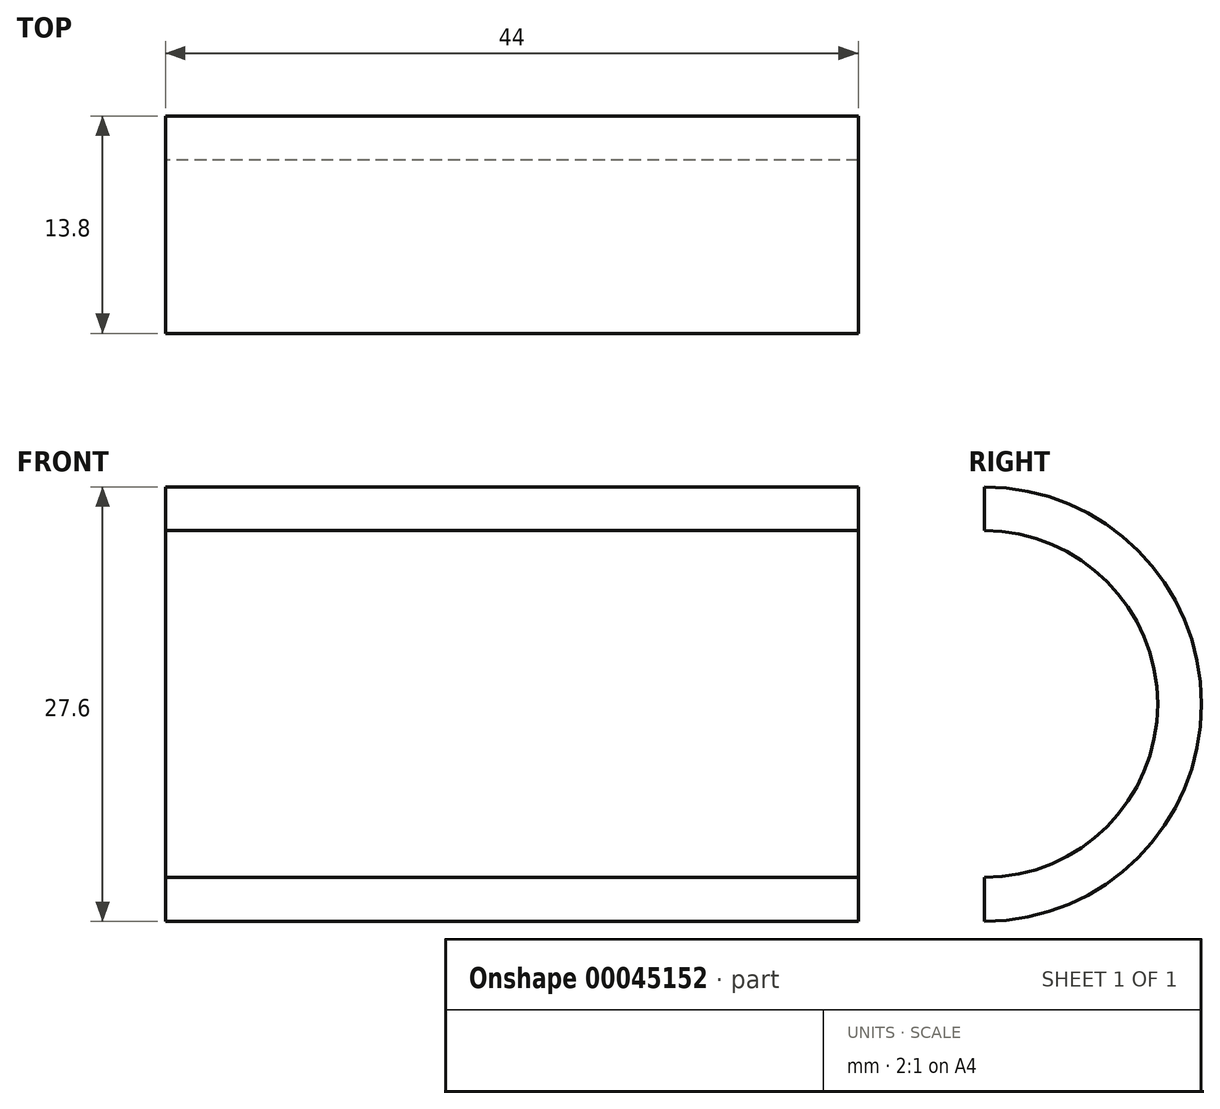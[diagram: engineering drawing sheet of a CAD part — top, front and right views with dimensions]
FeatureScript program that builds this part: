
annotation { "Feature Type Name" : "Feature", "Feature Type Description" : "" }
export const myFeature = defineFeature(function(context is Context, id is Id, definition is map)
    precondition{}
    {
        {
            var Q0;
            Q0=qCreatedBy(makeId("Right.planeOp"),FACE);
            var sketch = newSketch(context, id + "F0", { "sketchPlane" : qUnion([Q0])});
            skArc(sketch, "E0", {"start": v(0, -13.8) * mm, "mid": v(13.8, 0) * mm, "end": v(0, 13.8) * mm});
            skLineSegment(sketch, "E1", {"start": v(0, 13.8) * mm, "end": v(0, -13.8) * mm});
            skLineSegment(sketch, "E2", {"start": v(0, 0) * mm, "end": v(13.8, 0) * mm, "construction": true});
            skSolve(sketch);
        }
        {
            var Q0;
            Q0 = qSketchRegion(id + "F0", true);
            extrude(context, id + "F1", {"entities" : qUnion([Q0]), "depth" : 44 * mm});
        }
        {
            var Q0;
            Q0=qCreatedBy(makeId("Right.planeOp"),FACE);
            var sketch = newSketch(context, id + "F2", { "sketchPlane" : qUnion([Q0])});
            skArc(sketch, "E3", {"start": v(0, -11.01) * mm, "mid": v(11.01, 0) * mm, "end": v(0, 11.01) * mm});
            skLineSegment(sketch, "E4", {"start": v(0, 11.01) * mm, "end": v(0, -11.01) * mm});
            skLineSegment(sketch, "E5", {"start": v(0, 0) * mm, "end": v(11.01, 0) * mm, "construction": true});
            skSolve(sketch);
        }
        {
            var Q0;
            Q0 = qSketchRegion(id + "F2", true);
            extrude(context, id + "F3", {"entities" : qUnion([Q0]), "operationType" : NewBodyOperationType.REMOVE, "depth" : 44 * mm});
        }
    });
